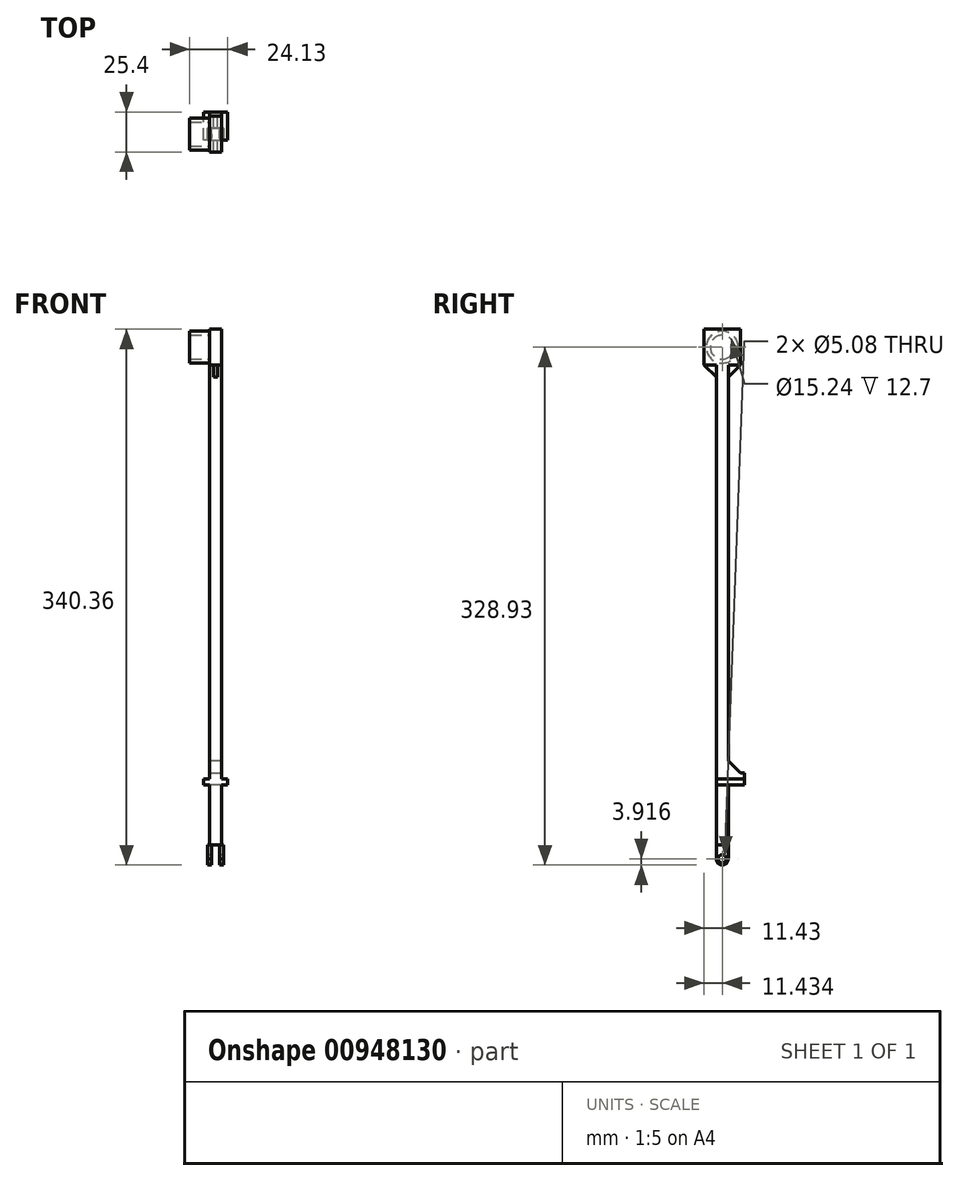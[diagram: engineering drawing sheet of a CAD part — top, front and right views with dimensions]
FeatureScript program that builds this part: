
annotation { "Feature Type Name" : "Feature", "Feature Type Description" : "" }
export const myFeature = defineFeature(function(context is Context, id is Id, definition is map)
    precondition{}
    {
        {
            var Q0;
            Q0=qCreatedBy(makeId("Top.planeOp"),FACE);
            var sketch = newSketch(context, id + "F0", { "sketchPlane" : qUnion([Q0])});
            skLineSegment(sketch, "E0.bottom", {"start": v(-35.84, -4.8) * mm, "end": v(-28.22, -4.8) * mm});
            skLineSegment(sketch, "E0.top", {"start": v(-35.84, -12.43) * mm, "end": v(-28.22, -12.43) * mm});
            skLineSegment(sketch, "E0.left", {"start": v(-35.84, -4.8) * mm, "end": v(-35.84, -12.43) * mm});
            skLineSegment(sketch, "E0.right", {"start": v(-28.22, -4.8) * mm, "end": v(-28.22, -12.43) * mm});
            skLineSegment(sketch, "E1.bottom", {"start": v(-29.49, -4.8) * mm, "end": v(-26.95, -4.8) * mm});
            skLineSegment(sketch, "E1.top", {"start": v(-29.49, -12.44) * mm, "end": v(-26.95, -12.44) * mm});
            skLineSegment(sketch, "E1.left", {"start": v(-29.49, -4.8) * mm, "end": v(-29.49, -12.44) * mm});
            skLineSegment(sketch, "E1.right", {"start": v(-26.95, -4.8) * mm, "end": v(-26.95, -12.44) * mm});
            skLineSegment(sketch, "E2", {"start": v(-26.95, -12.44) * mm, "end": v(-28.22, -12.43) * mm});
            skLineSegment(sketch, "E3", {"start": v(-29.49, -12.44) * mm, "end": v(-28.22, -12.43) * mm});
            skLineSegment(sketch, "E4", {"start": v(-29.49, -4.8) * mm, "end": v(-28.22, -4.8) * mm});
            skLineSegment(sketch, "E5.bottom", {"start": v(-34.57, -12.43) * mm, "end": v(-37.1, -12.43) * mm});
            skLineSegment(sketch, "E5.top", {"start": v(-34.57, -4.8) * mm, "end": v(-37.1, -4.8) * mm});
            skLineSegment(sketch, "E5.left", {"start": v(-34.57, -12.43) * mm, "end": v(-34.57, -4.8) * mm});
            skLineSegment(sketch, "E5.right", {"start": v(-37.1, -12.43) * mm, "end": v(-37.1, -4.8) * mm});
            skSolve(sketch);
        }
        {
            var Q0;
            Q0=makeQuery(id+"F0.imprint","IMPRINT",FACE,{"disambiguationData":[TD([[makeQuery(id+"F0.imprint","IMPRINT",EDGE,{"derivedFrom":sQuery(id+"F0.wireOp",EDGE,"E0.bottom")}),-1.0]])]});
            var Q1;
            {var subQ0=sQuery(id+"F0.wireOp",EDGE,"E0.right");Q1=makeQuery(id+"F0.imprint","IMPRINT",FACE,{"disambiguationData":[TD([[makeQuery(id+"F0.imprint","IMPRINT",EDGE,{"derivedFrom":subQ0}),-1.0]])]});}
            extrude(context, id + "F1", {"entities" : qUnion([Q0, Q1]), "depth" : 304.8 * mm, "offsetDistance" : 25.4 * mm});
        }
        {
            var Q0;
            Q0=makeQuery(id+"F0.imprint","IMPRINT",FACE,{"disambiguationData":[TD([[makeQuery(id+"F0.imprint","IMPRINT",EDGE,{"derivedFrom":sQuery(id+"F0.wireOp",EDGE,"E0.right")}),1.0]])]});
            var Q1;
            {var subQ0=sQuery(id+"F0.wireOp",EDGE,"E0.right");Q1=makeQuery(id+"F0.imprint","IMPRINT",FACE,{"disambiguationData":[TD([[makeQuery(id+"F0.imprint","IMPRINT",EDGE,{"derivedFrom":subQ0}),-1.0]])]});}
            var Q2;
            {var subQ0=sQuery(id+"F0.wireOp",EDGE,"E0.left");Q2=makeQuery(id+"F0.imprint","IMPRINT",FACE,{"disambiguationData":[TD([[makeQuery(id+"F0.imprint","IMPRINT",EDGE,{"derivedFrom":subQ0}),1.0]])]});}
            var Q3;
            {var subQ1=sQuery(id+"F0.wireOp",EDGE,"E0.left");Q3=makeQuery(id+"F0.imprint","IMPRINT",FACE,{"disambiguationData":[TD([[makeQuery(id+"F0.imprint","IMPRINT",EDGE,{"derivedFrom":subQ1}),-1.0]])]});}
            extrude(context, id + "F2", {"entities" : qUnion([Q0, Q1, Q2, Q3]), "operationType" : NewBodyOperationType.ADD, "oppositeDirection" : true, "depth" : 12.7 * mm, "offsetDistance" : 25.4 * mm});
        }
        {
            var Q0;
            Q0=makeQuery(id+"F2.opExtrude","SWEPT_FACE",FACE,{"disambiguationData":[OSD([sQuery(id+"F0.wireOp",EDGE,"E5.right")])]});
            var sketch = newSketch(context, id + "F3", { "sketchPlane" : qUnion([Q0])});
            skCircle(sketch, "E6", {"center": v(8.62, -8.78) * mm, "radius": 2.54 * mm});
            skPoint(sketch, "E6.centerSnap0", {"position": v(8.62, -12.7) * mm});
            skArc(sketch, "E7", {"start": v(8.62, -12.7) * mm, "mid": v(11.35, -11.55) * mm, "end": v(12.43, -8.78) * mm});
            skArc(sketch, "E8", {"start": v(4.8, -8.88) * mm, "mid": v(5.92, -11.58) * mm, "end": v(8.62, -12.7) * mm});
            skSolve(sketch);
        }
        {
            var Q0;
            {var subQ0=sQuery(id+"F3.wireOp",EDGE,"E7");var subQ1=sQuery(id+"F0.wireOp",EDGE,"E5.right");var subQ4=makeQuery(id+"F2.opExtrude","SWEPT_EDGE",EDGE,{"disambiguationData":[OSD([sQuery(id+"F0.wireOp",EDGE,"E5.bottom"),subQ1])]});var subQ5=makeQuery(id+"F3.imprint","INTERSECT",VERTEX,{"disambiguationData":[OD(1.0)],"derivedFrom":[subQ4,subQ0]});Q0=makeQuery(id+"F3.imprint","IMPRINT",FACE,{"disambiguationData":[TD([[makeQuery(id+"F3.imprint","IMPRINT",EDGE,{"disambiguationData":[TD([[subQ5,1.0]])],"derivedFrom":subQ0}),-1.0]])]});}
            var Q1;
            {var subQ0=sQuery(id+"F3.wireOp",EDGE,"E8");var subQ1=sQuery(id+"F0.wireOp",EDGE,"E5.right");var subQ2=makeQuery(id+"F2.opExtrude","CAP_EDGE",EDGE,{"disambiguationData":[OSD([subQ1])],"isStart":false});var subQ3=makeQuery(id+"F3.imprint","INTERSECT",VERTEX,{"derivedFrom":[subQ2,subQ0]});var subQ4=makeQuery(id+"F2.opExtrude","SWEPT_EDGE",EDGE,{"disambiguationData":[OSD([sQuery(id+"F0.wireOp",EDGE,"E5.top"),subQ1])]});var subQ5=makeQuery(id+"F3.imprint","INTERSECT",VERTEX,{"disambiguationData":[OD(1.0)],"derivedFrom":[subQ4,subQ0]});Q1=makeQuery(id+"F3.imprint","IMPRINT",FACE,{"disambiguationData":[TD([[makeQuery(id+"F3.imprint","IMPRINT",EDGE,{"disambiguationData":[TD([[subQ3,1.0],[subQ5,-1.0]])],"derivedFrom":subQ0}),-1.0]])]});}
            extrude(context, id + "F4", {"entities" : qUnion([Q0, Q1]), "operationType" : NewBodyOperationType.REMOVE, "oppositeDirection" : true, "depth" : 25.4 * mm, "offsetDistance" : 25.4 * mm});
        }
        {
            var Q0;
            Q0=makeQuery(id+"F3.imprint","IMPRINT",FACE,{"disambiguationData":[TD([[makeQuery(id+"F3.imprint","IMPRINT",EDGE,{"derivedFrom":sQuery(id+"F3.wireOp",EDGE,"E6")}),1.0]])]});
            extrude(context, id + "F5", {"entities" : qUnion([Q0]), "operationType" : NewBodyOperationType.REMOVE, "oppositeDirection" : true, "depth" : 25.4 * mm, "offsetDistance" : 25.4 * mm});
        }
        {
            var Q0;
            {var subQ0=sQuery(id+"F0.wireOp",EDGE,"E4");Q0=makeQuery(id+"F2.boolean.opBoolean","MERGE",FACE,{"derivedFrom":[makeQuery(id+"F1.opExtrude","SWEPT_FACE",FACE,{"disambiguationData":[OSD([sQuery(id+"F0.wireOp",EDGE,"E0.bottom"),subQ0])]}),makeQuery(id+"F2.opExtrude","SWEPT_FACE",FACE,{"disambiguationData":[OSD([sQuery(id+"F0.wireOp",EDGE,"E1.bottom"),subQ0])]})]});}
            var sketch = newSketch(context, id + "F6", { "sketchPlane" : qUnion([Q0])});
            skLineSegment(sketch, "E9.bottom", {"start": v(28.22, 38.1) * mm, "end": v(35.84, 38.1) * mm});
            skLineSegment(sketch, "E9.top", {"start": v(28.22, 45.72) * mm, "end": v(35.84, 45.72) * mm});
            skLineSegment(sketch, "E9.left", {"start": v(28.22, 38.1) * mm, "end": v(28.22, 45.72) * mm});
            skLineSegment(sketch, "E9.right", {"start": v(35.84, 38.1) * mm, "end": v(35.84, 45.72) * mm});
            skSolve(sketch);
        }
        {
            var Q0;
            Q0=makeQuery(id+"F6.imprint","IMPRINT",FACE,{"disambiguationData":[TD([[makeQuery(id+"F6.imprint","IMPRINT",EDGE,{"derivedFrom":sQuery(id+"F6.wireOp",EDGE,"E9.bottom")}),1.0]])]});
            extrude(context, id + "F7", {"entities" : qUnion([Q0]), "operationType" : NewBodyOperationType.ADD, "depth" : 10.16 * mm, "offsetDistance" : 25.4 * mm});
        }
        {
            var Q0;
            Q0=makeQuery(id+"F7.boolean.opBoolean","MERGE",FACE,{"derivedFrom":[makeQuery(id+"F1.opExtrude","SWEPT_FACE",FACE,{"disambiguationData":[OSD([sQuery(id+"F0.wireOp",EDGE,"E0.right")])]}),makeQuery(id+"F7.opExtrude","SWEPT_FACE",FACE,{"disambiguationData":[OSD([sQuery(id+"F6.wireOp",EDGE,"E9.left")])]})]});
            var sketch = newSketch(context, id + "F8", { "sketchPlane" : qUnion([Q0])});
            skLineSegment(sketch, "E10.bottom", {"start": v(-12.43, 38.1) * mm, "end": v(5.35, 38.1) * mm});
            skLineSegment(sketch, "E10.top", {"start": v(-12.43, 41.91) * mm, "end": v(5.35, 41.91) * mm});
            skLineSegment(sketch, "E10.left", {"start": v(-12.43, 38.1) * mm, "end": v(-12.43, 41.91) * mm});
            skLineSegment(sketch, "E10.right", {"start": v(5.35, 38.1) * mm, "end": v(5.35, 41.91) * mm});
            skSolve(sketch);
        }
        {
            var Q0;
            Q0=makeQuery(id+"F8.imprint","IMPRINT",FACE,{"disambiguationData":[TD([[makeQuery(id+"F8.imprint","IMPRINT",EDGE,{"derivedFrom":sQuery(id+"F8.wireOp",EDGE,"E10.top")}),-1.0]])]});
            extrude(context, id + "F9", {"entities" : qUnion([Q0]), "operationType" : NewBodyOperationType.ADD, "depth" : 3.8 * mm, "offsetDistance" : 25.4 * mm, "hasSecondDirection" : true, "secondDirectionOppositeDirection" : true, "secondDirectionDepth" : 11.43 * mm});
        }
        {
            var Q0;
            Q0=makeQuery(id+"F1.opExtrude","CAP_FACE",FACE,{"disambiguationData":[OSD([sQuery(id+"F0.wireOp",EDGE,"E0.bottom"),sQuery(id+"F0.wireOp",EDGE,"E0.top"),sQuery(id+"F0.wireOp",EDGE,"E0.left"),sQuery(id+"F0.wireOp",EDGE,"E0.right"),sQuery(id+"F0.wireOp",EDGE,"E4"),sQuery(id+"F0.wireOp",EDGE,"E5.bottom")])],"isStart":false});
            var sketch = newSketch(context, id + "F10", { "sketchPlane" : qUnion([Q0])});
            skPoint(sketch, "E11.middle", {"position": v(-32.03, -8.62) * mm});
            skPoint(sketch, "E11.middle.positionSnap0", {"position": v(-32.03, -12.43) * mm});
            skPoint(sketch, "E11.centerSnap0", {"position": v(-32.03, -12.43) * mm});
            skLineSegment(sketch, "E12.bottom", {"start": v(-28.22, 2.81) * mm, "end": v(-35.84, 2.81) * mm});
            skLineSegment(sketch, "E12.top", {"start": v(-28.22, -20.05) * mm, "end": v(-35.84, -20.05) * mm});
            skLineSegment(sketch, "E12.left", {"start": v(-28.22, 2.81) * mm, "end": v(-28.22, -20.05) * mm});
            skLineSegment(sketch, "E12.right", {"start": v(-35.84, 2.81) * mm, "end": v(-35.84, -20.05) * mm});
            skSolve(sketch);
        }
        {
            var Q0;
            {var subQ0=sQuery(id+"F10.wireOp",EDGE,"E12.top");Q0=makeQuery(id+"F10.imprint","IMPRINT",FACE,{"disambiguationData":[TD([[makeQuery(id+"F10.imprint","IMPRINT",EDGE,{"derivedFrom":subQ0}),-1.0]])]});}
            var Q1;
            {var subQ2=makeQuery(id+"F1.opExtrude","CAP_EDGE",EDGE,{"disambiguationData":[OSD([sQuery(id+"F0.wireOp",EDGE,"E0.bottom"),sQuery(id+"F0.wireOp",EDGE,"E4")])],"isStart":false});Q1=makeQuery(id+"F10.imprint","IMPRINT",FACE,{"disambiguationData":[TD([[makeQuery(id+"F10.imprint","IMPRINT",EDGE,{"derivedFrom":subQ2}),-1.0]])]});}
            var Q2;
            {var subQ0=sQuery(id+"F10.wireOp",EDGE,"E12.bottom");Q2=makeQuery(id+"F10.imprint","IMPRINT",FACE,{"disambiguationData":[TD([[makeQuery(id+"F10.imprint","IMPRINT",EDGE,{"derivedFrom":subQ0}),1.0]])]});}
            extrude(context, id + "F11", {"entities" : qUnion([Q0, Q1, Q2]), "operationType" : NewBodyOperationType.ADD, "depth" : 22.86 * mm, "offsetDistance" : 25.4 * mm});
        }
        {
            var Q0;
            {var subQ2=sQuery(id+"F0.wireOp",EDGE,"E0.right");var subQ5=sQuery(id+"F6.wireOp",EDGE,"E9.left");var subQ6=sQuery(id+"F6.wireOp",EDGE,"E9.top");Q0=makeQuery(id+"F11.boolean.opBoolean","MERGE",FACE,{"derivedFrom":[makeQuery(id+"F9.boolean.opBoolean","SPLIT",FACE,{"disambiguationData":[TD([makeQuery(id+"F7.opExtrude","SWEPT_FACE",FACE,{"disambiguationData":[OSD([subQ6])]})])],"derivedFrom":makeQuery(id+"F7.boolean.opBoolean","MERGE",FACE,{"derivedFrom":[makeQuery(id+"F1.opExtrude","SWEPT_FACE",FACE,{"disambiguationData":[OSD([subQ2])]}),makeQuery(id+"F7.opExtrude","SWEPT_FACE",FACE,{"disambiguationData":[OSD([subQ5])]})]})}),makeQuery(id+"F11.opExtrude","SWEPT_FACE",FACE,{"disambiguationData":[OSD([sQuery(id+"F10.wireOp",EDGE,"E12.left")])]})]});}
            var sketch = newSketch(context, id + "F12", { "sketchPlane" : qUnion([Q0])});
            skCircle(sketch, "E13", {"center": v(-8.62, 316.23) * mm, "radius": 7.62 * mm});
            skPoint(sketch, "E13.centerSnap0", {"position": v(-20.05, 316.23) * mm});
            skCircle(sketch, "E14", {"center": v(-8.62, 316.23) * mm, "radius": 10.16 * mm});
            skSolve(sketch);
        }
        {
            var Q0;
            Q0=makeQuery(id+"F12.imprint","IMPRINT",FACE,{"disambiguationData":[TD([[makeQuery(id+"F12.imprint","IMPRINT",EDGE,{"derivedFrom":sQuery(id+"F12.wireOp",EDGE,"E13")}),-1.0]])]});
            extrude(context, id + "F13", {"entities" : qUnion([Q0]), "operationType" : NewBodyOperationType.ADD, "oppositeDirection" : true, "depth" : 20.32 * mm, "offsetDistance" : 25.4 * mm});
        }
        {
            var Q0;
            {var subQ0=sQuery(id+"F10.wireOp",EDGE,"E12.top");var subQ2=sQuery(id+"F10.wireOp",EDGE,"E12.left");var subQ3=sQuery(id+"F0.wireOp",EDGE,"E0.top");var subQ4=sQuery(id+"F10.wireOp",EDGE,"E12.right");Q0=makeQuery(id+"F11.boolean.opBoolean","SPLIT",FACE,{"disambiguationData":[TD([makeQuery(id+"F2.opExtrude","SWEPT_FACE",FACE,{"disambiguationData":[OSD([subQ3])]})])],"derivedFrom":makeQuery(id+"F11.opExtrude","CAP_FACE",FACE,{"disambiguationData":[OSD([sQuery(id+"F10.wireOp",EDGE,"E12.bottom"),subQ0,subQ2,subQ4])],"isStart":true})});}
            var sketch = newSketch(context, id + "F14", { "sketchPlane" : qUnion([Q0])});
            skLineSegment(sketch, "E15.bottom", {"start": v(-33.3, 20.05) * mm, "end": v(-30.76, 20.05) * mm});
            skLineSegment(sketch, "E15.top", {"start": v(-33.3, 12.43) * mm, "end": v(-30.76, 12.43) * mm});
            skLineSegment(sketch, "E15.left", {"start": v(-33.3, 20.05) * mm, "end": v(-33.3, 12.43) * mm});
            skLineSegment(sketch, "E15.right", {"start": v(-30.76, 20.05) * mm, "end": v(-30.76, 12.43) * mm});
            skSolve(sketch);
        }
        {
            var Q0;
            Q0=makeQuery(id+"F14.imprint","IMPRINT",FACE,{"disambiguationData":[TD([[makeQuery(id+"F14.imprint","IMPRINT",EDGE,{"derivedFrom":sQuery(id+"F14.wireOp",EDGE,"E15.bottom")}),1.0]])]});
            extrude(context, id + "F15", {"entities" : qUnion([Q0]), "operationType" : NewBodyOperationType.ADD, "depth" : 7.62 * mm, "offsetDistance" : 25.4 * mm});
        }
        {
            var Q0;
            Q0=makeQuery(id+"F15.opExtrude","SWEPT_FACE",FACE,{"disambiguationData":[OSD([sQuery(id+"F14.wireOp",EDGE,"E15.right")])]});
            var sketch = newSketch(context, id + "F16", { "sketchPlane" : qUnion([Q0])});
            skLineSegment(sketch, "E16", {"start": v(-20.05, 304.8) * mm, "end": v(-12.43, 297.18) * mm});
            skSolve(sketch);
        }
        {
            var Q0;
            Q0=makeQuery(id+"F16.imprint","IMPRINT",FACE,{"disambiguationData":[TD([[makeQuery(id+"F16.imprint","IMPRINT",EDGE,{"derivedFrom":sQuery(id+"F16.wireOp",EDGE,"E16")}),-1.0]])]});
            extrude(context, id + "F17", {"entities" : qUnion([Q0]), "operationType" : NewBodyOperationType.REMOVE, "oppositeDirection" : true, "depth" : 25.4 * mm, "offsetDistance" : 25.4 * mm});
        }
        {
            var Q0;
            {var subQ1=sQuery(id+"F10.wireOp",EDGE,"E12.right");var subQ2=sQuery(id+"F10.wireOp",EDGE,"E12.bottom");var subQ3=sQuery(id+"F10.wireOp",EDGE,"E12.left");Q0=makeQuery(id+"F11.boolean.opBoolean","SPLIT",FACE,{"disambiguationData":[TD([makeQuery(id+"F11.opExtrude","SWEPT_FACE",FACE,{"disambiguationData":[OSD([subQ2])]})])],"derivedFrom":makeQuery(id+"F11.opExtrude","CAP_FACE",FACE,{"disambiguationData":[OSD([subQ2,sQuery(id+"F10.wireOp",EDGE,"E12.top"),subQ3,subQ1])],"isStart":true})});}
            var sketch = newSketch(context, id + "F18", { "sketchPlane" : qUnion([Q0])});
            skLineSegment(sketch, "E17.bottom", {"start": v(-30.76, 4.8) * mm, "end": v(-33.3, 4.8) * mm});
            skLineSegment(sketch, "E17.top", {"start": v(-30.76, -2.81) * mm, "end": v(-33.3, -2.81) * mm});
            skLineSegment(sketch, "E17.left", {"start": v(-30.76, 4.8) * mm, "end": v(-30.76, -2.81) * mm});
            skLineSegment(sketch, "E17.right", {"start": v(-33.3, 4.8) * mm, "end": v(-33.3, -2.81) * mm});
            skSolve(sketch);
        }
        {
            var Q0;
            Q0=makeQuery(id+"F18.imprint","IMPRINT",FACE,{"disambiguationData":[TD([[makeQuery(id+"F18.imprint","IMPRINT",EDGE,{"derivedFrom":sQuery(id+"F18.wireOp",EDGE,"E17.bottom")}),-1.0]])]});
            extrude(context, id + "F19", {"entities" : qUnion([Q0]), "operationType" : NewBodyOperationType.ADD, "depth" : 7.62 * mm, "offsetDistance" : 25.4 * mm});
        }
        {
            var Q0;
            Q0=makeQuery(id+"F19.opExtrude","SWEPT_FACE",FACE,{"disambiguationData":[OSD([sQuery(id+"F18.wireOp",EDGE,"E17.left")])]});
            var sketch = newSketch(context, id + "F20", { "sketchPlane" : qUnion([Q0])});
            skLineSegment(sketch, "E18", {"start": v(2.81, 304.8) * mm, "end": v(-4.8, 297.18) * mm});
            skSolve(sketch);
        }
        {
            var Q0;
            Q0=makeQuery(id+"F20.imprint","IMPRINT",FACE,{"disambiguationData":[TD([[makeQuery(id+"F20.imprint","IMPRINT",EDGE,{"derivedFrom":sQuery(id+"F20.wireOp",EDGE,"E18")}),1.0]])]});
            extrude(context, id + "F21", {"entities" : qUnion([Q0]), "operationType" : NewBodyOperationType.REMOVE, "oppositeDirection" : true, "depth" : 25.4 * mm, "offsetDistance" : 25.4 * mm});
        }
        {
            var Q0;
            Q0=makeQuery(id+"F7.opExtrude","SWEPT_FACE",FACE,{"disambiguationData":[OSD([sQuery(id+"F6.wireOp",EDGE,"E9.top")])]});
            var sketch = newSketch(context, id + "F22", { "sketchPlane" : qUnion([Q0])});
            skLineSegment(sketch, "E19", {"start": v(-35.84, 2.81) * mm, "end": v(-28.22, 2.81) * mm});
            skSolve(sketch);
        }
        {
            var Q0;
            {var subQ0=sQuery(id+"F22.wireOp",EDGE,"E19");Q0=makeQuery(id+"F22.imprint","IMPRINT",FACE,{"disambiguationData":[TD([[makeQuery(id+"F22.imprint","IMPRINT",EDGE,{"derivedFrom":subQ0}),-1.0]])]});}
            extrude(context, id + "F23", {"entities" : qUnion([Q0]), "operationType" : NewBodyOperationType.ADD, "depth" : 7.62 * mm, "offsetDistance" : 25.4 * mm});
        }
        {
            var Q0;
            {var subQ0=sQuery(id+"F6.wireOp",EDGE,"E9.left");var subQ1=sQuery(id+"F6.wireOp",EDGE,"E9.top");var subQ2=sQuery(id+"F0.wireOp",EDGE,"E4");var subQ3=sQuery(id+"F0.wireOp",EDGE,"E1.bottom");var subQ4=sQuery(id+"F0.wireOp",EDGE,"E0.right");Q0=makeQuery(id+"F23.boolean.opBoolean","MERGE",FACE,{"derivedFrom":[makeQuery(id+"F11.boolean.opBoolean","MERGE",FACE,{"derivedFrom":[makeQuery(id+"F9.boolean.opBoolean","SPLIT",FACE,{"disambiguationData":[TD([makeQuery(id+"F7.opExtrude","SWEPT_FACE",FACE,{"disambiguationData":[OSD([subQ1])]})])],"derivedFrom":makeQuery(id+"F7.boolean.opBoolean","MERGE",FACE,{"derivedFrom":[makeQuery(id+"F1.opExtrude","SWEPT_FACE",FACE,{"disambiguationData":[OSD([subQ4])]}),makeQuery(id+"F7.opExtrude","SWEPT_FACE",FACE,{"disambiguationData":[OSD([subQ0])]})]})}),makeQuery(id+"F11.opExtrude","SWEPT_FACE",FACE,{"disambiguationData":[OSD([sQuery(id+"F10.wireOp",EDGE,"E12.left")])]})]}),makeQuery(id+"F23.opExtrude","SWEPT_FACE",FACE,{"disambiguationData":[OSD([subQ4,subQ3,subQ2,subQ1,subQ0])]})]});}
            var sketch = newSketch(context, id + "F24", { "sketchPlane" : qUnion([Q0])});
            skLineSegment(sketch, "E20", {"start": v(-4.8, 53.34) * mm, "end": v(2.81, 45.72) * mm});
            skSolve(sketch);
        }
        {
            var Q0;
            Q0=makeQuery(id+"F24.imprint","IMPRINT",FACE,{"disambiguationData":[TD([[makeQuery(id+"F24.imprint","IMPRINT",EDGE,{"derivedFrom":sQuery(id+"F24.wireOp",EDGE,"E20")}),1.0]])]});
            extrude(context, id + "F25", {"entities" : qUnion([Q0]), "operationType" : NewBodyOperationType.REMOVE, "oppositeDirection" : true, "depth" : 25.4 * mm, "offsetDistance" : 25.4 * mm});
        }
    });
